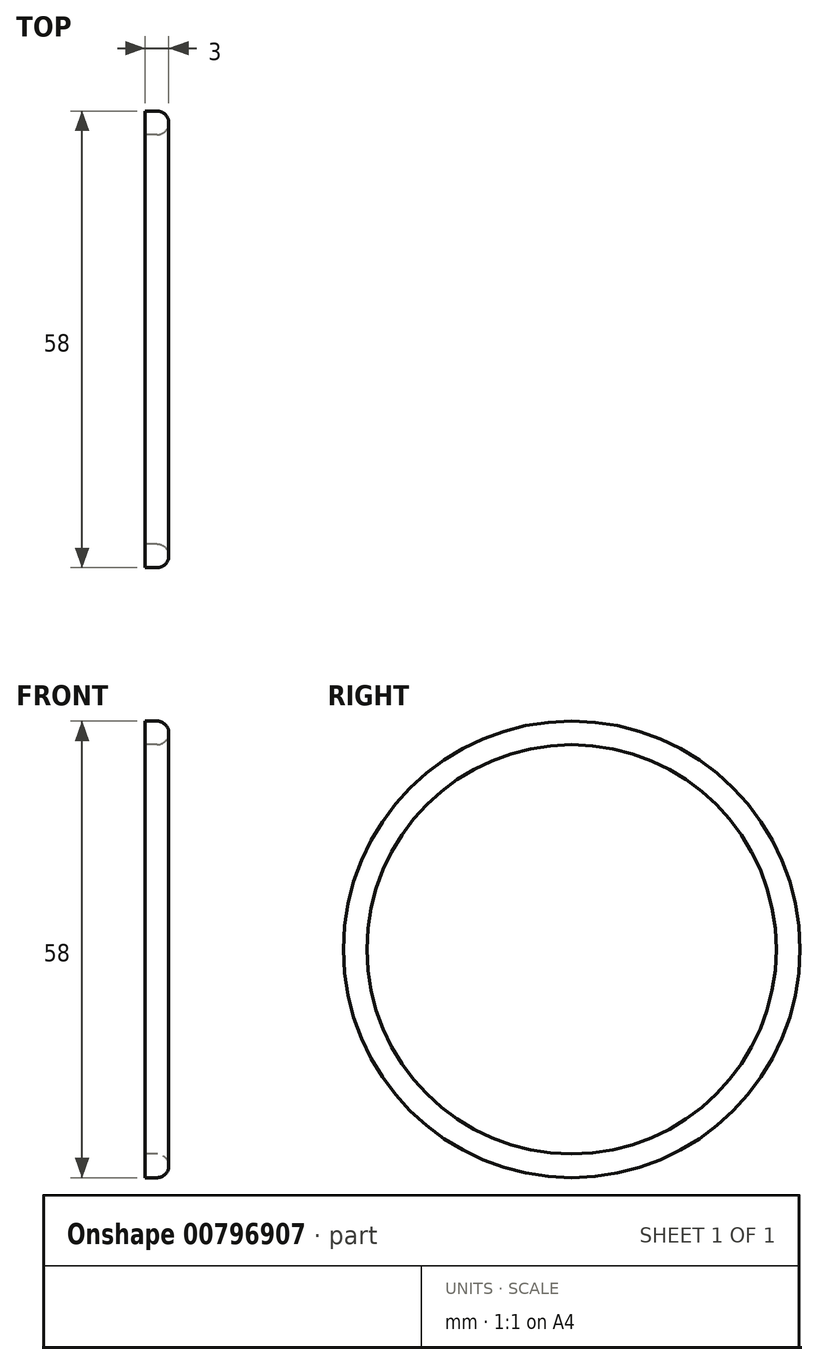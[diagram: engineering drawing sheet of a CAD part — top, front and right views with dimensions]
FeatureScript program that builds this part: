
annotation { "Feature Type Name" : "Feature", "Feature Type Description" : "" }
export const myFeature = defineFeature(function(context is Context, id is Id, definition is map)
    precondition{}
    {
        {
            var Q0;
            Q0=qCreatedBy(makeId("Right.planeOp"),FACE);
            var sketch = newSketch(context, id + "F0", { "sketchPlane" : qUnion([Q0])});
            skCircle(sketch, "E0", {"center": v(-28.04, 32.91) * mm, "radius": 14.75 * mm});
            skCircle(sketch, "E1", {"center": v(-28.04, 32.91) * mm, "radius": 2.5 * mm});
            skCircle(sketch, "E2", {"center": v(-28.04, 32.91) * mm, "radius": 32 * mm});
            skCircle(sketch, "E3", {"center": v(-28.04, 32.91) * mm, "radius": 29 * mm});
            skCircle(sketch, "E4", {"center": v(-28.04, 32.91) * mm, "radius": 26 * mm});
            skSolve(sketch);
        }
        {
            var Q0;
            Q0=makeQuery(id+"F0.imprint","IMPRINT",FACE,{"disambiguationData":[TD([[makeQuery(id+"F0.imprint","IMPRINT",EDGE,{"derivedFrom":sQuery(id+"F0.wireOp",EDGE,"E3")}),1.0]])]});
            extrude(context, id + "F1", {"entities" : qUnion([Q0]), "depth" : 3 * mm, "offsetDistance" : 25 * mm});
        }
        {
            var Q0;
            Q0=makeQuery(id+"F1.opExtrude","CAP_EDGE",EDGE,{"disambiguationData":[OSD([sQuery(id+"F0.wireOp",EDGE,"E3")])],"isStart":false});
            var Q1;
            Q1=makeQuery(id+"F1.opExtrude","CAP_EDGE",EDGE,{"disambiguationData":[OSD([sQuery(id+"F0.wireOp",EDGE,"E4")])],"isStart":false});
            fillet(context, id + "F2", {"entities" : qUnion([Q0, Q1]), "radius" : 1.5 * mm, "tangentPropagation" : true, "allowEdgeOverflow" : false});
        }
    });
